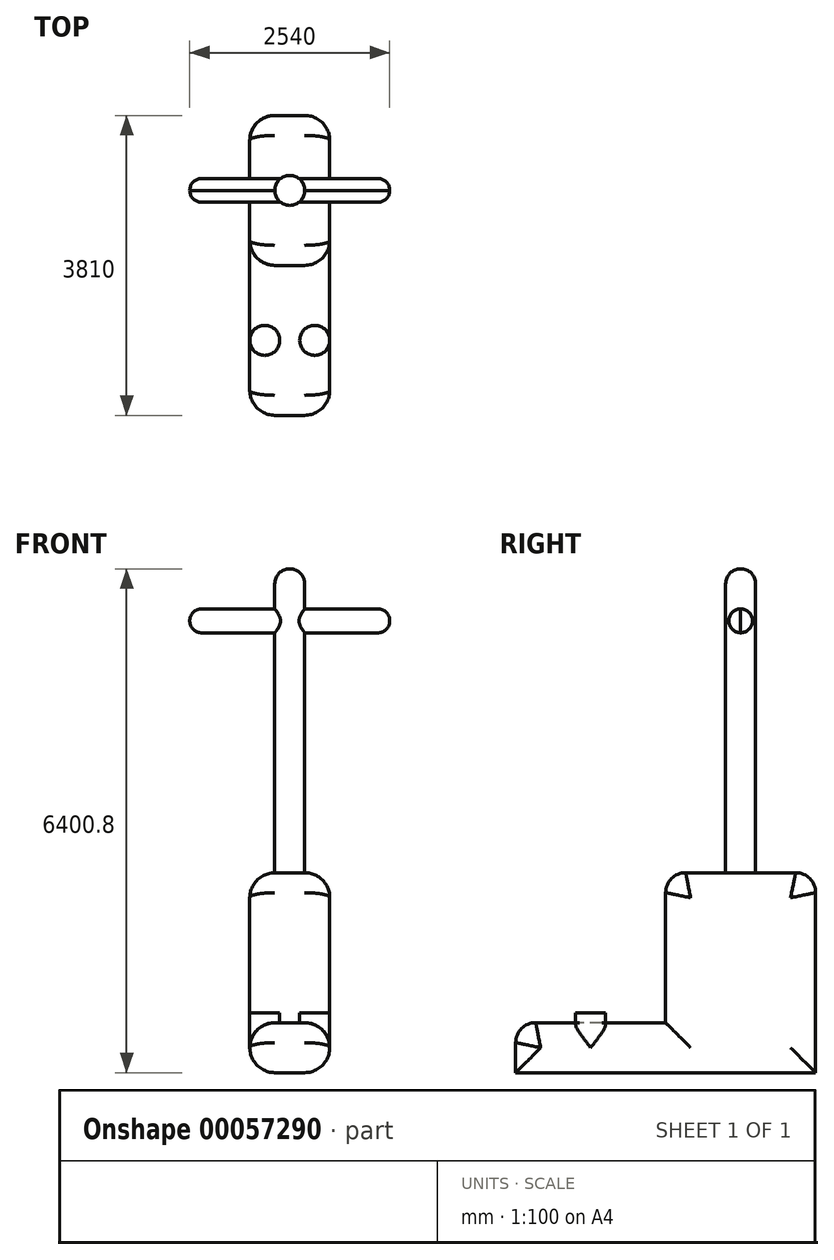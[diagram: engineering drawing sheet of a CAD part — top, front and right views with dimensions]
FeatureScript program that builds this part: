
annotation { "Feature Type Name" : "Feature", "Feature Type Description" : "" }
export const myFeature = defineFeature(function(context is Context, id is Id, definition is map)
    precondition{}
    {
        {
            var Q0;
            Q0=qCreatedBy(makeId("Top.planeOp"),FACE);
            var sketch = newSketch(context, id + "F0", { "sketchPlane" : qUnion([Q0])});
            skLineSegment(sketch, "E0.rect.bottom", {"start": v(-508, -1905) * mm, "end": v(508, -1905) * mm});
            skLineSegment(sketch, "E0.rect.top", {"start": v(-508, 1905) * mm, "end": v(508, 1905) * mm});
            skLineSegment(sketch, "E0.rect.left", {"start": v(-508, -1905) * mm, "end": v(-508, 1905) * mm});
            skLineSegment(sketch, "E0.rect.right", {"start": v(508, -1905) * mm, "end": v(508, 1905) * mm});
            skPoint(sketch, "E0.rect.middle", {"position": v(0, 0) * mm});
            skSolve(sketch);
        }
        {
            var Q0;
            Q0=makeQuery(id+"F0.imprint","IMPRINT",FACE,{"disambiguationData":[TD([[makeQuery(id+"F0.imprint","IMPRINT",EDGE,{"derivedFrom":sQuery(id+"F0.wireOp",EDGE,"E0.rect.bottom")}),1.0]])]});
            extrude(context, id + "F1", {"entities" : qUnion([Q0]), "depth" : 635 * mm});
        }
        {
            var Q0;
            Q0=makeQuery(id+"F1.opExtrude","CAP_FACE",FACE,{"disambiguationData":[OSD([sQuery(id+"F0.wireOp",EDGE,"E0.rect.bottom"),sQuery(id+"F0.wireOp",EDGE,"E0.rect.top"),sQuery(id+"F0.wireOp",EDGE,"E0.rect.left"),sQuery(id+"F0.wireOp",EDGE,"E0.rect.right")])],"isStart":false});
            var sketch = newSketch(context, id + "F2", { "sketchPlane" : qUnion([Q0])});
            skLineSegment(sketch, "E1.bottom", {"start": v(-508, 1905) * mm, "end": v(508, 1905) * mm});
            skLineSegment(sketch, "E1.top", {"start": v(-508, 0) * mm, "end": v(508, 0) * mm});
            skLineSegment(sketch, "E1.left", {"start": v(-508, 1905) * mm, "end": v(-508, 0) * mm});
            skLineSegment(sketch, "E1.right", {"start": v(508, 1905) * mm, "end": v(508, 0) * mm});
            skSolve(sketch);
        }
        {
            var Q0;
            Q0=makeQuery(id+"F2.imprint","IMPRINT",FACE,{"disambiguationData":[TD([[makeQuery(id+"F2.imprint","IMPRINT",EDGE,{"derivedFrom":sQuery(id+"F2.wireOp",EDGE,"E1.bottom")}),-1.0]])]});
            extrude(context, id + "F3", {"entities" : qUnion([Q0]), "operationType" : NewBodyOperationType.ADD, "depth" : 1905 * mm});
        }
        {
            var Q0;
            Q0=makeQuery(id+"F1.opExtrude","CAP_FACE",FACE,{"disambiguationData":[OSD([sQuery(id+"F0.wireOp",EDGE,"E0.rect.bottom"),sQuery(id+"F0.wireOp",EDGE,"E0.rect.top"),sQuery(id+"F0.wireOp",EDGE,"E0.rect.left"),sQuery(id+"F0.wireOp",EDGE,"E0.rect.right")])],"isStart":false});
            var sketch = newSketch(context, id + "F4", { "sketchPlane" : qUnion([Q0])});
            skPoint(sketch, "E2.centerSnap0", {"position": v(508, -952.5) * mm});
            skCircle(sketch, "E3", {"center": v(-317.5, -952.5) * mm, "radius": 190.5 * mm});
            skCircle(sketch, "E4", {"center": v(317.5, -952.5) * mm, "radius": 190.5 * mm});
            skSolve(sketch);
        }
        {
            var Q0;
            Q0=makeQuery(id+"F4.imprint","IMPRINT",FACE,{"disambiguationData":[TD([[makeQuery(id+"F4.imprint","IMPRINT",EDGE,{"derivedFrom":sQuery(id+"F4.wireOp",EDGE,"E3")}),1.0]])]});
            var Q1;
            Q1=makeQuery(id+"F4.imprint","IMPRINT",FACE,{"disambiguationData":[TD([[makeQuery(id+"F4.imprint","IMPRINT",EDGE,{"derivedFrom":sQuery(id+"F4.wireOp",EDGE,"E4")}),1.0]])]});
            extrude(context, id + "F5", {"entities" : qUnion([Q0, Q1]), "operationType" : NewBodyOperationType.ADD, "depth" : 127 * mm});
        }
        {
            var Q0;
            Q0=makeQuery(id+"F3.boolean.opBoolean","MERGE",FACE,{"derivedFrom":[makeQuery(id+"F1.opExtrude","SWEPT_FACE",FACE,{"disambiguationData":[OSD([sQuery(id+"F0.wireOp",EDGE,"E0.rect.left")])]}),makeQuery(id+"F3.opExtrude","SWEPT_FACE",FACE,{"disambiguationData":[OSD([sQuery(id+"F2.wireOp",EDGE,"E1.left")])]})]});
            var Q1;
            Q1=makeQuery(id+"F3.boolean.opBoolean","MERGE",FACE,{"derivedFrom":[makeQuery(id+"F1.opExtrude","SWEPT_FACE",FACE,{"disambiguationData":[OSD([sQuery(id+"F0.wireOp",EDGE,"E0.rect.right")])]}),makeQuery(id+"F3.opExtrude","SWEPT_FACE",FACE,{"disambiguationData":[OSD([sQuery(id+"F2.wireOp",EDGE,"E1.right")])]})]});
            fillet(context, id + "F6", {"entities" : qUnion([Q0, Q1]), "radius" : 317.5 * mm, "tangentPropagation" : true, "allowEdgeOverflow" : false});
        }
        {
            var Q0;
            Q0=makeQuery(id+"F3.opExtrude","CAP_FACE",FACE,{"disambiguationData":[OSD([sQuery(id+"F2.wireOp",EDGE,"E1.bottom"),sQuery(id+"F2.wireOp",EDGE,"E1.top"),sQuery(id+"F2.wireOp",EDGE,"E1.left"),sQuery(id+"F2.wireOp",EDGE,"E1.right")])],"isStart":false});
            var sketch = newSketch(context, id + "F7", { "sketchPlane" : qUnion([Q0])});
            skCircle(sketch, "E5", {"center": v(0, 952.5) * mm, "radius": 190.5 * mm});
            skPoint(sketch, "E5.centerSnap0", {"position": v(-190.5, 952.5) * mm});
            skSolve(sketch);
        }
        {
            var Q0;
            {var subQ0=sQuery(id+"F7.wireOp",EDGE,"E5");var subQ1=sQuery(id+"F2.wireOp",EDGE,"E1.right");var subQ2=sQuery(id+"F2.wireOp",EDGE,"E1.left");var subQ3=makeQuery(id+"F3.opExtrude","CAP_FACE",FACE,{"disambiguationData":[OSD([sQuery(id+"F2.wireOp",EDGE,"E1.bottom"),sQuery(id+"F2.wireOp",EDGE,"E1.top"),subQ2,subQ1])],"isStart":false});var subQ4=makeQuery(id+"F7.imprint","INTERSECT",VERTEX,{"derivedFrom":[makeQuery(id+"F6.opFillet","BLEND_EDGE",EDGE,{"blendedFrom":[makeQuery(id+"F3.opExtrude","CAP_EDGE",EDGE,{"disambiguationData":[OSD([subQ2])],"isStart":false}),subQ3],"blendedInto":[subQ3]}),subQ0]});Q0=makeQuery(id+"F7.imprint","IMPRINT",FACE,{"disambiguationData":[TD([[makeQuery(id+"F7.imprint","IMPRINT",EDGE,{"disambiguationData":[TD([[subQ4,1.0]])],"derivedFrom":subQ0}),1.0]])]});}
            extrude(context, id + "F8", {"entities" : qUnion([Q0]), "operationType" : NewBodyOperationType.ADD, "depth" : 3048 * mm});
        }
        {
            var Q0;
            Q0=makeQuery(id+"F8.opExtrude","CAP_FACE",FACE,{"disambiguationData":[OSD([sQuery(id+"F7.wireOp",EDGE,"E5")])],"isStart":false});
            var sketch = newSketch(context, id + "F9", { "sketchPlane" : qUnion([Q0])});
            skLineSegment(sketch, "E6.rect.bottom", {"start": v(-1270, 1102.54) * mm, "end": v(1270, 1102.54) * mm});
            skLineSegment(sketch, "E6.rect.top", {"start": v(-1270, 802.46) * mm, "end": v(1270, 802.46) * mm});
            skLineSegment(sketch, "E6.rect.left", {"start": v(-1270, 1102.54) * mm, "end": v(-1270, 802.46) * mm});
            skLineSegment(sketch, "E6.rect.right", {"start": v(1270, 1102.54) * mm, "end": v(1270, 802.46) * mm});
            skPoint(sketch, "E6.rect.middle", {"position": v(0, 952.5) * mm});
            skSolve(sketch);
        }
        {
            var Q0;
            {var subQ0=sQuery(id+"F9.wireOp",EDGE,"E6.rect.right");Q0=makeQuery(id+"F9.imprint","IMPRINT",FACE,{"disambiguationData":[TD([[makeQuery(id+"F9.imprint","IMPRINT",EDGE,{"derivedFrom":subQ0}),-1.0]])]});}
            var Q1;
            {var subQ0=sQuery(id+"F9.wireOp",EDGE,"E6.rect.bottom");var subQ1=makeQuery(id+"F8.opExtrude","CAP_EDGE",EDGE,{"disambiguationData":[OSD([sQuery(id+"F7.wireOp",EDGE,"E5")])],"isStart":false});var subQ2=makeQuery(id+"F9.imprint","INTERSECT",VERTEX,{"disambiguationData":[OD(0.0)],"derivedFrom":[subQ1,subQ0]});Q1=makeQuery(id+"F9.imprint","IMPRINT",FACE,{"disambiguationData":[TD([[makeQuery(id+"F9.imprint","IMPRINT",EDGE,{"disambiguationData":[TD([[subQ2,-1.0]])],"derivedFrom":subQ0}),-1.0]])]});}
            var Q2;
            {var subQ0=sQuery(id+"F9.wireOp",EDGE,"E6.rect.left");Q2=makeQuery(id+"F9.imprint","IMPRINT",FACE,{"disambiguationData":[TD([[makeQuery(id+"F9.imprint","IMPRINT",EDGE,{"derivedFrom":subQ0}),1.0]])]});}
            var Q3;
            {var subQ0=sQuery(id+"F9.wireOp",EDGE,"E6.rect.top");var subQ1=makeQuery(id+"F8.opExtrude","CAP_EDGE",EDGE,{"disambiguationData":[OSD([sQuery(id+"F7.wireOp",EDGE,"E5")])],"isStart":false});var subQ2=makeQuery(id+"F9.imprint","INTERSECT",VERTEX,{"disambiguationData":[OD(0.0)],"derivedFrom":[subQ1,subQ0]});Q3=makeQuery(id+"F9.imprint","IMPRINT",FACE,{"disambiguationData":[TD([[makeQuery(id+"F9.imprint","IMPRINT",EDGE,{"disambiguationData":[TD([[subQ2,-1.0]])],"derivedFrom":subQ0}),-1.0]])]});}
            var Q4;
            {var subQ0=sQuery(id+"F9.wireOp",EDGE,"E6.rect.bottom");var subQ1=makeQuery(id+"F8.opExtrude","CAP_EDGE",EDGE,{"disambiguationData":[OSD([sQuery(id+"F7.wireOp",EDGE,"E5")])],"isStart":false});var subQ2=makeQuery(id+"F9.imprint","INTERSECT",VERTEX,{"disambiguationData":[OD(0.0)],"derivedFrom":[subQ1,subQ0]});Q4=makeQuery(id+"F9.imprint","IMPRINT",FACE,{"disambiguationData":[TD([[makeQuery(id+"F9.imprint","IMPRINT",EDGE,{"disambiguationData":[TD([[subQ2,-1.0]])],"derivedFrom":subQ0}),1.0]])]});}
            extrude(context, id + "F10", {"entities" : qUnion([Q0, Q1, Q2, Q3, Q4]), "operationType" : NewBodyOperationType.ADD, "depth" : 304.8 * mm});
        }
        {
            var Q0;
            Q0=makeQuery(id+"F10.opExtrude","CAP_FACE",FACE,{"disambiguationData":[OSD([sQuery(id+"F7.wireOp",EDGE,"E5"),sQuery(id+"F9.wireOp",EDGE,"E6.rect.bottom"),sQuery(id+"F9.wireOp",EDGE,"E6.rect.top"),sQuery(id+"F9.wireOp",EDGE,"E6.rect.left"),sQuery(id+"F9.wireOp",EDGE,"E6.rect.right")])],"isStart":false});
            var sketch = newSketch(context, id + "F11", { "sketchPlane" : qUnion([Q0])});
            skCircle(sketch, "E7", {"center": v(0, 952.5) * mm, "radius": 190.5 * mm});
            skSolve(sketch);
        }
        {
            var Q0;
            {var subQ0=sQuery(id+"F11.wireOp",EDGE,"E7");var subQ1=sQuery(id+"F9.wireOp",EDGE,"E6.rect.left");var subQ2=sQuery(id+"F9.wireOp",EDGE,"E6.rect.bottom");var subQ4=makeQuery(id+"F11.imprint","INTERSECT",VERTEX,{"derivedFrom":[makeQuery(id+"F10.opExtrude","CAP_EDGE",EDGE,{"disambiguationData":[OSD([subQ2]),TDD([makeQuery(id+"F9.imprint","IMPRINT",EDGE,{"disambiguationData":[TD([[makeQuery(id+"F9.imprint","INTERSECT",VERTEX,{"derivedFrom":[subQ2,subQ1]}),-1.0]])],"derivedFrom":subQ2})])],"isStart":false}),subQ0]});Q0=makeQuery(id+"F11.imprint","IMPRINT",FACE,{"disambiguationData":[TD([[makeQuery(id+"F11.imprint","IMPRINT",EDGE,{"disambiguationData":[TD([[subQ4,1.0]])],"derivedFrom":subQ0}),1.0]])]});}
            extrude(context, id + "F12", {"entities" : qUnion([Q0]), "operationType" : NewBodyOperationType.ADD, "depth" : 508 * mm});
        }
        {
            var Q0;
            Q0=makeQuery(id+"F1.opExtrude","CAP_EDGE",EDGE,{"disambiguationData":[OSD([sQuery(id+"F0.wireOp",EDGE,"E0.rect.bottom")])],"isStart":false});
            var Q1;
            Q1=makeQuery(id+"F3.opExtrude","CAP_EDGE",EDGE,{"disambiguationData":[OSD([sQuery(id+"F2.wireOp",EDGE,"E1.top")])],"isStart":true});
            var Q2;
            Q2=makeQuery(id+"F3.opExtrude","CAP_EDGE",EDGE,{"disambiguationData":[OSD([sQuery(id+"F2.wireOp",EDGE,"E1.top")])],"isStart":false});
            var Q3;
            Q3=makeQuery(id+"F3.opExtrude","CAP_EDGE",EDGE,{"disambiguationData":[OSD([sQuery(id+"F2.wireOp",EDGE,"E1.bottom")])],"isStart":false});
            fillet(context, id + "F13", {"entities" : qUnion([Q0, Q1, Q2, Q3]), "radius" : 254 * mm, "tangentPropagation" : true, "allowEdgeOverflow" : false});
        }
        {
            var Q0;
            {var subQ0=sQuery(id+"F9.wireOp",EDGE,"E6.rect.top");Q0=makeQuery(id+"F10.opExtrude","CAP_EDGE",EDGE,{"disambiguationData":[OSD([subQ0]),TDD([makeQuery(id+"F9.imprint","IMPRINT",EDGE,{"disambiguationData":[TD([[makeQuery(id+"F9.imprint","INTERSECT",VERTEX,{"derivedFrom":[subQ0,sQuery(id+"F9.wireOp",EDGE,"E6.rect.left")]}),-1.0]])],"derivedFrom":subQ0})])],"isStart":true});}
            var Q1;
            {var subQ0=sQuery(id+"F9.wireOp",EDGE,"E6.rect.top");Q1=makeQuery(id+"F10.opExtrude","CAP_EDGE",EDGE,{"disambiguationData":[OSD([subQ0]),TDD([makeQuery(id+"F9.imprint","IMPRINT",EDGE,{"disambiguationData":[TD([[makeQuery(id+"F9.imprint","INTERSECT",VERTEX,{"derivedFrom":[subQ0,sQuery(id+"F9.wireOp",EDGE,"E6.rect.left")]}),-1.0]])],"derivedFrom":subQ0})])],"isStart":false});}
            var Q2;
            {var subQ0=sQuery(id+"F9.wireOp",EDGE,"E6.rect.bottom");Q2=makeQuery(id+"F10.opExtrude","CAP_EDGE",EDGE,{"disambiguationData":[OSD([subQ0]),TDD([makeQuery(id+"F9.imprint","IMPRINT",EDGE,{"disambiguationData":[TD([[makeQuery(id+"F9.imprint","INTERSECT",VERTEX,{"derivedFrom":[subQ0,sQuery(id+"F9.wireOp",EDGE,"E6.rect.left")]}),-1.0]])],"derivedFrom":subQ0})])],"isStart":true});}
            var Q3;
            {var subQ0=sQuery(id+"F9.wireOp",EDGE,"E6.rect.bottom");Q3=makeQuery(id+"F10.opExtrude","CAP_EDGE",EDGE,{"disambiguationData":[OSD([subQ0]),TDD([makeQuery(id+"F9.imprint","IMPRINT",EDGE,{"disambiguationData":[TD([[makeQuery(id+"F9.imprint","INTERSECT",VERTEX,{"derivedFrom":[subQ0,sQuery(id+"F9.wireOp",EDGE,"E6.rect.left")]}),-1.0]])],"derivedFrom":subQ0})])],"isStart":false});}
            var Q4;
            {var subQ0=sQuery(id+"F9.wireOp",EDGE,"E6.rect.top");Q4=makeQuery(id+"F10.opExtrude","CAP_EDGE",EDGE,{"disambiguationData":[OSD([subQ0]),TDD([makeQuery(id+"F9.imprint","IMPRINT",EDGE,{"disambiguationData":[TD([[makeQuery(id+"F9.imprint","INTERSECT",VERTEX,{"derivedFrom":[subQ0,sQuery(id+"F9.wireOp",EDGE,"E6.rect.right")]}),1.0]])],"derivedFrom":subQ0})])],"isStart":false});}
            var Q5;
            {var subQ0=sQuery(id+"F9.wireOp",EDGE,"E6.rect.bottom");Q5=makeQuery(id+"F10.opExtrude","CAP_EDGE",EDGE,{"disambiguationData":[OSD([subQ0]),TDD([makeQuery(id+"F9.imprint","IMPRINT",EDGE,{"disambiguationData":[TD([[makeQuery(id+"F9.imprint","INTERSECT",VERTEX,{"derivedFrom":[subQ0,sQuery(id+"F9.wireOp",EDGE,"E6.rect.right")]}),1.0]])],"derivedFrom":subQ0})])],"isStart":false});}
            var Q6;
            {var subQ0=sQuery(id+"F9.wireOp",EDGE,"E6.rect.bottom");Q6=makeQuery(id+"F10.opExtrude","CAP_EDGE",EDGE,{"disambiguationData":[OSD([subQ0]),TDD([makeQuery(id+"F9.imprint","IMPRINT",EDGE,{"disambiguationData":[TD([[makeQuery(id+"F9.imprint","INTERSECT",VERTEX,{"derivedFrom":[subQ0,sQuery(id+"F9.wireOp",EDGE,"E6.rect.right")]}),1.0]])],"derivedFrom":subQ0})])],"isStart":true});}
            var Q7;
            {var subQ0=sQuery(id+"F9.wireOp",EDGE,"E6.rect.top");Q7=makeQuery(id+"F10.opExtrude","CAP_EDGE",EDGE,{"disambiguationData":[OSD([subQ0]),TDD([makeQuery(id+"F9.imprint","IMPRINT",EDGE,{"disambiguationData":[TD([[makeQuery(id+"F9.imprint","INTERSECT",VERTEX,{"derivedFrom":[subQ0,sQuery(id+"F9.wireOp",EDGE,"E6.rect.right")]}),1.0]])],"derivedFrom":subQ0})])],"isStart":true});}
            fillet(context, id + "F14", {"entities" : qUnion([Q0, Q1, Q2, Q3, Q4, Q5, Q6, Q7]), "radius" : 152.4 * mm, "tangentPropagation" : true, "allowEdgeOverflow" : false});
        }
        {
            var Q0;
            Q0=makeQuery(id+"F12.opExtrude","CAP_FACE",FACE,{"disambiguationData":[OSD([sQuery(id+"F11.wireOp",EDGE,"E7")])],"isStart":false});
            fillet(context, id + "F15", {"entities" : qUnion([Q0]), "radius" : 190.5 * mm, "tangentPropagation" : true, "allowEdgeOverflow" : false});
        }
        {
            var Q0;
            Q0=makeQuery(id+"F10.opExtrude","SWEPT_FACE",FACE,{"disambiguationData":[OSD([sQuery(id+"F9.wireOp",EDGE,"E6.rect.left")])]});
            var Q1;
            Q1=makeQuery(id+"F10.opExtrude","SWEPT_FACE",FACE,{"disambiguationData":[OSD([sQuery(id+"F9.wireOp",EDGE,"E6.rect.right")])]});
            fillet(context, id + "F16", {"entities" : qUnion([Q0, Q1]), "radius" : 149.86 * mm, "tangentPropagation" : true, "allowEdgeOverflow" : false});
        }
    });
